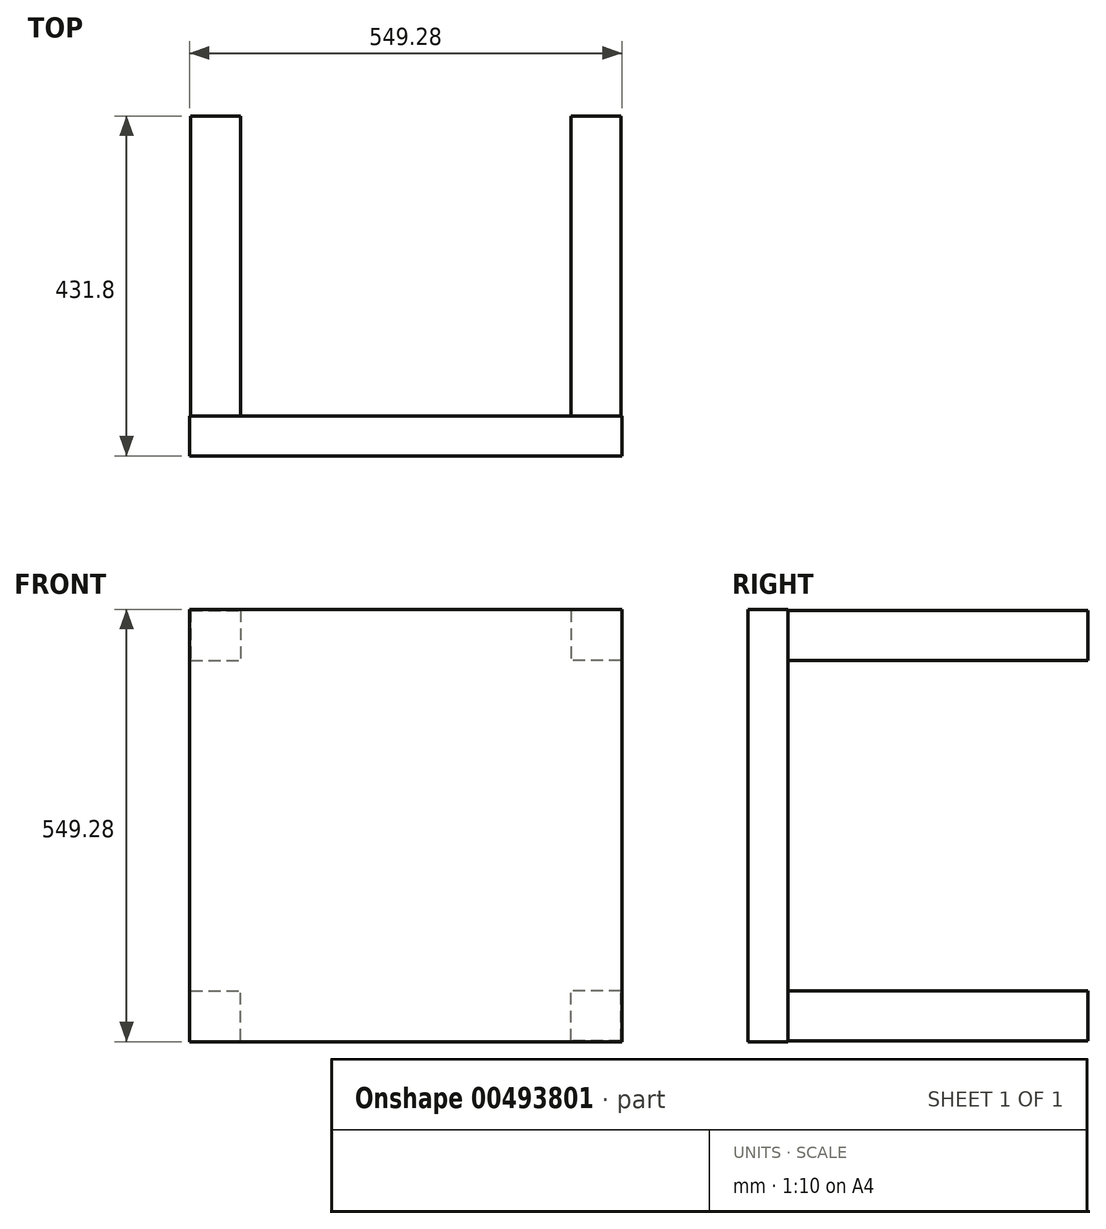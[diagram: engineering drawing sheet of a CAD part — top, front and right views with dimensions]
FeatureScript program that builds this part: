
annotation { "Feature Type Name" : "Feature", "Feature Type Description" : "" }
export const myFeature = defineFeature(function(context is Context, id is Id, definition is map)
    precondition{}
    {
        {
            var Q0;
            Q0=qCreatedBy(makeId("Front.planeOp"),FACE);
            var sketch = newSketch(context, id + "F0", { "sketchPlane" : qUnion([Q0])});
            skLineSegment(sketch, "E0.bottom", {"start": v(274.64, 274.64) * mm, "end": v(-274.64, 274.64) * mm});
            skLineSegment(sketch, "E0.top", {"start": v(274.64, -274.64) * mm, "end": v(-274.64, -274.64) * mm});
            skLineSegment(sketch, "E0.left", {"start": v(274.64, 274.64) * mm, "end": v(274.64, -274.64) * mm});
            skLineSegment(sketch, "E0.right", {"start": v(-274.64, 274.64) * mm, "end": v(-274.64, -274.64) * mm});
            skPoint(sketch, "E0.middle", {"position": v(0, 0) * mm});
            skLineSegment(sketch, "E1", {"start": v(-274.64, 274.64) * mm, "end": v(-273.37, 274.64) * mm, "construction": true});
            skLineSegment(sketch, "E2", {"start": v(-273.37, 274.64) * mm, "end": v(-273.37, 273.37) * mm, "construction": true});
            skPoint(sketch, "E3", {"position": v(-273.37, 273.37) * mm});
            skLineSegment(sketch, "E4.bottom", {"start": v(-273.37, 273.37) * mm, "end": v(-209.87, 273.37) * mm});
            skLineSegment(sketch, "E4.top", {"start": v(-273.37, 209.87) * mm, "end": v(-209.87, 209.87) * mm});
            skLineSegment(sketch, "E4.left", {"start": v(-273.37, 273.37) * mm, "end": v(-273.37, 209.87) * mm});
            skLineSegment(sketch, "E4.right", {"start": v(-209.87, 273.37) * mm, "end": v(-209.87, 209.87) * mm});
            skLineSegment(sketch, "E5", {"start": v(0, 0) * mm, "end": v(0, 20.48) * mm});
            skLineSegment(sketch, "E6", {"start": v(0, 20.48) * mm, "end": v(0, 0) * mm});
            skLineSegment(sketch, "E7", {"start": v(28.9, 0) * mm, "end": v(0, 0) * mm});
            skLineSegment(sketch, "E8.MirrorCS", {"start": v(209.87, 273.37) * mm, "end": v(209.87, 209.87) * mm});
            skLineSegment(sketch, "E9.MirrorCS", {"start": v(273.37, 209.87) * mm, "end": v(209.87, 209.87) * mm});
            skLineSegment(sketch, "E10.MirrorCS", {"start": v(273.37, 273.37) * mm, "end": v(273.37, 209.87) * mm});
            skLineSegment(sketch, "E11.MirrorCS", {"start": v(273.37, 273.37) * mm, "end": v(209.87, 273.37) * mm});
            skLineSegment(sketch, "E12.MirrorCS", {"start": v(-209.87, -273.37) * mm, "end": v(-209.87, -209.87) * mm});
            skLineSegment(sketch, "E13.MirrorCS", {"start": v(-273.37, -209.87) * mm, "end": v(-209.87, -209.87) * mm});
            skLineSegment(sketch, "E14.MirrorCS", {"start": v(-273.37, -273.37) * mm, "end": v(-273.37, -209.87) * mm});
            skLineSegment(sketch, "E15.MirrorCS", {"start": v(-273.37, -273.37) * mm, "end": v(-209.87, -273.37) * mm});
            skLineSegment(sketch, "E16.MirrorCS", {"start": v(273.37, -209.87) * mm, "end": v(209.87, -209.87) * mm});
            skLineSegment(sketch, "E17.MirrorCS", {"start": v(209.87, -273.37) * mm, "end": v(209.87, -209.87) * mm});
            skLineSegment(sketch, "E18.MirrorCS", {"start": v(273.37, -273.37) * mm, "end": v(273.37, -209.87) * mm});
            skLineSegment(sketch, "E19.MirrorCS", {"start": v(273.37, -273.37) * mm, "end": v(209.87, -273.37) * mm});
            skSolve(sketch);
        }
        {
            var Q0;
            Q0=makeQuery(id+"F0.imprint","IMPRINT",FACE,{"disambiguationData":[TD([[makeQuery(id+"F0.imprint","IMPRINT",EDGE,{"derivedFrom":sQuery(id+"F0.wireOp",EDGE,"E0.bottom")}),1.0]])]});
            var Q1;
            Q1=makeQuery(id+"F0.imprint","IMPRINT",FACE,{"disambiguationData":[TD([[makeQuery(id+"F0.imprint","IMPRINT",EDGE,{"derivedFrom":sQuery(id+"F0.wireOp",EDGE,"E8.MirrorCS")}),1.0]])]});
            var Q2;
            Q2=makeQuery(id+"F0.imprint","IMPRINT",FACE,{"disambiguationData":[TD([[makeQuery(id+"F0.imprint","IMPRINT",EDGE,{"derivedFrom":sQuery(id+"F0.wireOp",EDGE,"E4.bottom")}),-1.0]])]});
            var Q3;
            Q3=makeQuery(id+"F0.imprint","IMPRINT",FACE,{"disambiguationData":[TD([[makeQuery(id+"F0.imprint","IMPRINT",EDGE,{"derivedFrom":sQuery(id+"F0.wireOp",EDGE,"E12.MirrorCS")}),1.0]])]});
            var Q4;
            Q4=makeQuery(id+"F0.imprint","IMPRINT",FACE,{"disambiguationData":[TD([[makeQuery(id+"F0.imprint","IMPRINT",EDGE,{"derivedFrom":sQuery(id+"F0.wireOp",EDGE,"E16.MirrorCS")}),1.0]])]});
            extrude(context, id + "F1", {"entities" : qUnion([Q0, Q1, Q2, Q3, Q4]), "depth" : 50.8 * mm});
        }
        {
            var Q0;
            Q0=makeQuery(id+"F0.imprint","IMPRINT",FACE,{"disambiguationData":[TD([[makeQuery(id+"F0.imprint","IMPRINT",EDGE,{"derivedFrom":sQuery(id+"F0.wireOp",EDGE,"E4.bottom")}),-1.0]])]});
            var Q1;
            Q1=makeQuery(id+"F0.imprint","IMPRINT",FACE,{"disambiguationData":[TD([[makeQuery(id+"F0.imprint","IMPRINT",EDGE,{"derivedFrom":sQuery(id+"F0.wireOp",EDGE,"E8.MirrorCS")}),1.0]])]});
            var Q2;
            Q2=makeQuery(id+"F0.imprint","IMPRINT",FACE,{"disambiguationData":[TD([[makeQuery(id+"F0.imprint","IMPRINT",EDGE,{"derivedFrom":sQuery(id+"F0.wireOp",EDGE,"E16.MirrorCS")}),1.0]])]});
            var Q3;
            Q3=makeQuery(id+"F0.imprint","IMPRINT",FACE,{"disambiguationData":[TD([[makeQuery(id+"F0.imprint","IMPRINT",EDGE,{"derivedFrom":sQuery(id+"F0.wireOp",EDGE,"E12.MirrorCS")}),1.0]])]});
            extrude(context, id + "F2", {"entities" : qUnion([Q0, Q1, Q2, Q3]), "operationType" : NewBodyOperationType.ADD, "oppositeDirection" : true, "depth" : 381 * mm});
        }
    });
